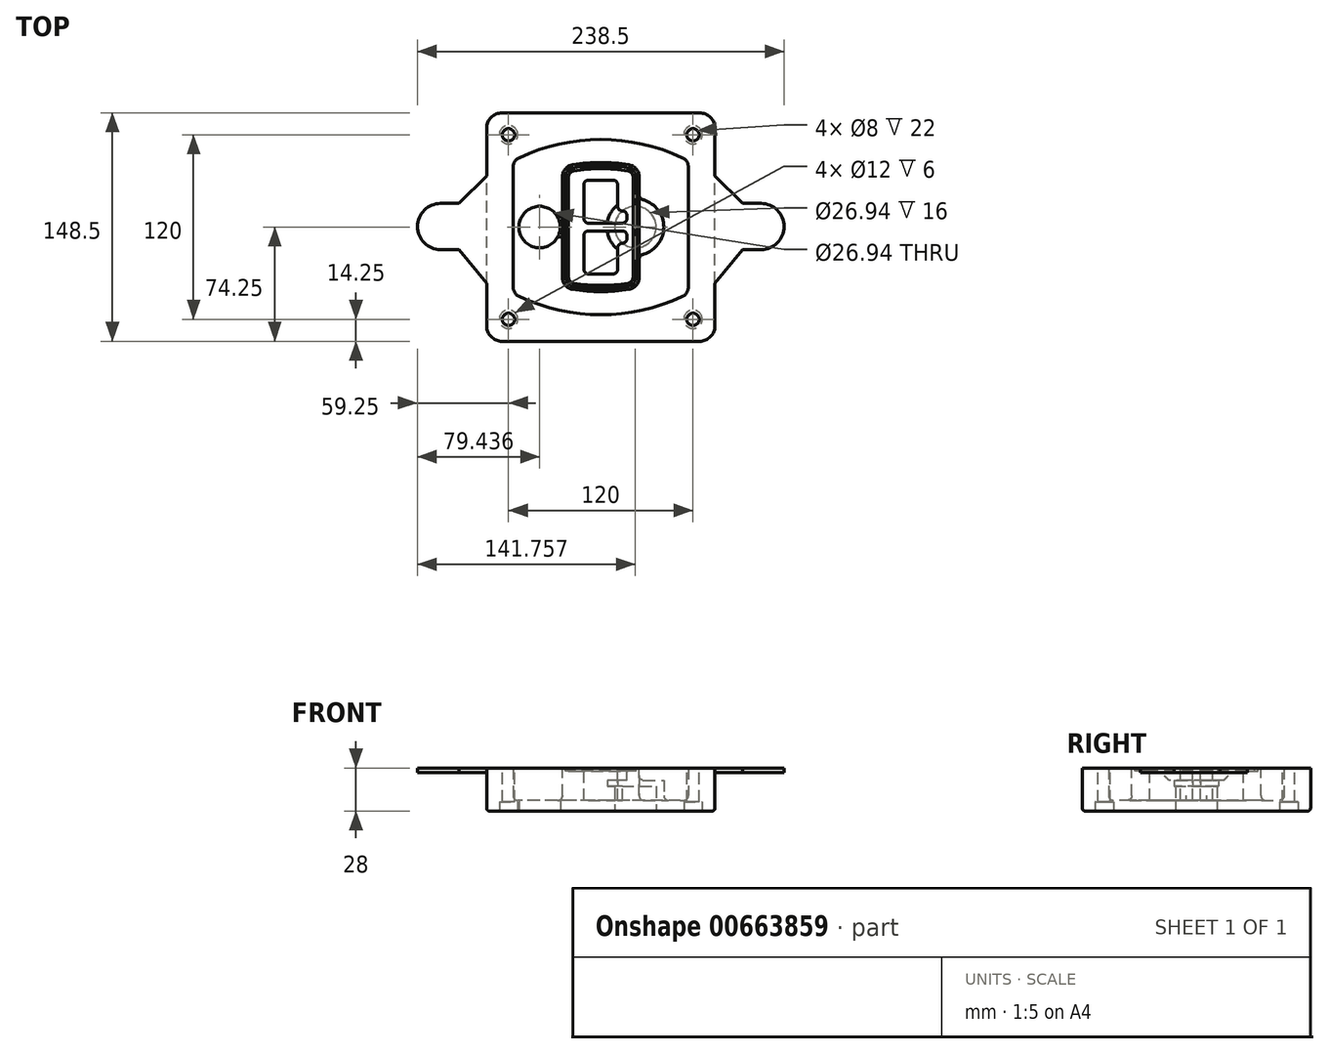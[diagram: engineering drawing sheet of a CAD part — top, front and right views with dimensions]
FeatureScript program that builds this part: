
annotation { "Feature Type Name" : "Feature", "Feature Type Description" : "" }
export const myFeature = defineFeature(function(context is Context, id is Id, definition is map)
    precondition{}
    {
        {
            var Q0;
            Q0=qCreatedBy(makeId("Top.planeOp"),FACE);
            var sketch = newSketch(context, id + "F0", { "sketchPlane" : qUnion([Q0])});
            skPoint(sketch, "E0.rect.middle", {"position": v(0, 0) * mm});
            skLineSegment(sketch, "E1.bottom", {"start": v(-64.25, -74.25) * mm, "end": v(64.25, -74.25) * mm});
            skLineSegment(sketch, "E1.top", {"start": v(-64.25, 74.25) * mm, "end": v(64.25, 74.25) * mm});
            skLineSegment(sketch, "E1.left", {"start": v(-74.25, -64.25) * mm, "end": v(-74.25, 64.25) * mm});
            skLineSegment(sketch, "E1.right", {"start": v(74.25, -64.25) * mm, "end": v(74.25, 64.25) * mm});
            skLineSegment(sketch, "E2", {"start": v(-74.25, 74.25) * mm, "end": v(74.25, -74.25) * mm, "construction": true});
            skLineSegment(sketch, "E3", {"start": v(74.25, 74.25) * mm, "end": v(-74.25, -74.25) * mm, "construction": true});
            skCircle(sketch, "E4", {"center": v(-60, 60) * mm, "radius": 4 * mm});
            skCircle(sketch, "E5", {"center": v(60, 60) * mm, "radius": 4 * mm});
            skCircle(sketch, "E6", {"center": v(60, -60) * mm, "radius": 4 * mm});
            skCircle(sketch, "E7", {"center": v(-60, -60) * mm, "radius": 4 * mm});
            skLineSegment(sketch, "E8", {"start": v(-60, 60) * mm, "end": v(60, 60) * mm, "construction": true});
            skLineSegment(sketch, "E9", {"start": v(60, 60) * mm, "end": v(60, -60) * mm, "construction": true});
            skLineSegment(sketch, "E10", {"start": v(60, -60) * mm, "end": v(-60, -60) * mm, "construction": true});
            skLineSegment(sketch, "E11", {"start": v(-60, -60) * mm, "end": v(-60, 60) * mm, "construction": true});
            skLineSegment(sketch, "E12", {"start": v(-60, 38.83) * mm, "end": v(-60, -38.83) * mm});
            skLineSegment(sketch, "E13", {"start": v(60, 38.83) * mm, "end": v(60, -38.83) * mm});
            skArc(sketch, "E14", {"start": v(54.26, 47.88) * mm, "mid": v(0, 60) * mm, "end": v(-54.26, 47.88) * mm});
            skArc(sketch, "E15", {"start": v(-54.26, -47.88) * mm, "mid": v(0, -60) * mm, "end": v(54.26, -47.88) * mm});
            skLineSegment(sketch, "E16", {"start": v(-60, 0) * mm, "end": v(60, 0) * mm, "construction": true});
            skPoint(sketch, "E17.visualSharp", {"position": v(-60, -45) * mm});
            skArc(sketch, "E17.filletArc", {"start": v(-60, -38.83) * mm, "mid": v(-58.44, -44.2) * mm, "end": v(-54.26, -47.88) * mm});
            skPoint(sketch, "E18.visualSharp", {"position": v(-60, 45) * mm});
            skArc(sketch, "E18.filletArc", {"start": v(-54.26, 47.88) * mm, "mid": v(-58.44, 44.2) * mm, "end": v(-60, 38.83) * mm});
            skPoint(sketch, "E19.visualSharp", {"position": v(60, 45) * mm});
            skArc(sketch, "E19.filletArc", {"start": v(60, 38.83) * mm, "mid": v(58.44, 44.2) * mm, "end": v(54.26, 47.88) * mm});
            skPoint(sketch, "E20.visualSharp", {"position": v(60, -45) * mm});
            skArc(sketch, "E20.filletArc", {"start": v(54.26, -47.88) * mm, "mid": v(58.44, -44.2) * mm, "end": v(60, -38.83) * mm});
            skPoint(sketch, "E21.visualSharp", {"position": v(-74.25, 74.25) * mm});
            skArc(sketch, "E21.filletArc", {"start": v(-64.25, 74.25) * mm, "mid": v(-71.32, 71.32) * mm, "end": v(-74.25, 64.25) * mm});
            skPoint(sketch, "E22.visualSharp", {"position": v(74.25, 74.25) * mm});
            skArc(sketch, "E22.filletArc", {"start": v(74.25, 64.25) * mm, "mid": v(71.32, 71.32) * mm, "end": v(64.25, 74.25) * mm});
            skPoint(sketch, "E23.visualSharp", {"position": v(74.25, -74.25) * mm});
            skArc(sketch, "E23.filletArc", {"start": v(64.25, -74.25) * mm, "mid": v(71.32, -71.32) * mm, "end": v(74.25, -64.25) * mm});
            skPoint(sketch, "E24.visualSharp", {"position": v(-74.25, -74.25) * mm});
            skArc(sketch, "E24.filletArc", {"start": v(-74.25, -64.25) * mm, "mid": v(-71.32, -71.32) * mm, "end": v(-64.25, -74.25) * mm});
            skArc(sketch, "E25.0", {"start": v(57, 38.83) * mm, "mid": v(55.9, 42.58) * mm, "end": v(52.98, 45.17) * mm});
            skLineSegment(sketch, "E25.1", {"start": v(57, 38.83) * mm, "end": v(57, -38.83) * mm});
            skArc(sketch, "E25.2", {"start": v(52.98, -45.17) * mm, "mid": v(55.9, -42.58) * mm, "end": v(57, -38.83) * mm});
            skArc(sketch, "E25.3", {"start": v(-52.98, -45.17) * mm, "mid": v(0, -57) * mm, "end": v(52.98, -45.17) * mm});
            skArc(sketch, "E25.4", {"start": v(-57, -38.83) * mm, "mid": v(-55.9, -42.58) * mm, "end": v(-52.98, -45.17) * mm});
            skArc(sketch, "E25.5", {"start": v(52.98, 45.17) * mm, "mid": v(0, 57) * mm, "end": v(-52.98, 45.17) * mm});
            skLineSegment(sketch, "E25.6", {"start": v(-57, 38.83) * mm, "end": v(-57, -38.83) * mm});
            skArc(sketch, "E25.7", {"start": v(-52.98, 45.17) * mm, "mid": v(-55.9, 42.58) * mm, "end": v(-57, 38.83) * mm});
            skArc(sketch, "E26.0", {"start": v(-55.96, 51.5) * mm, "mid": v(-61.82, 46.33) * mm, "end": v(-64, 38.83) * mm});
            skArc(sketch, "E26.1", {"start": v(55.96, 51.5) * mm, "mid": v(0, 64) * mm, "end": v(-55.96, 51.5) * mm});
            skArc(sketch, "E26.2", {"start": v(64, 38.83) * mm, "mid": v(61.82, 46.33) * mm, "end": v(55.96, 51.5) * mm});
            skLineSegment(sketch, "E26.3", {"start": v(64, 38.83) * mm, "end": v(64, -38.83) * mm});
            skArc(sketch, "E26.4", {"start": v(55.96, -51.5) * mm, "mid": v(61.82, -46.33) * mm, "end": v(64, -38.83) * mm});
            skLineSegment(sketch, "E26.5", {"start": v(-64, 38.83) * mm, "end": v(-64, -38.83) * mm});
            skArc(sketch, "E26.6", {"start": v(-55.96, -51.5) * mm, "mid": v(0, -64) * mm, "end": v(55.96, -51.5) * mm});
            skArc(sketch, "E26.7", {"start": v(-64, -38.83) * mm, "mid": v(-61.82, -46.33) * mm, "end": v(-55.96, -51.5) * mm});
            skSolve(sketch);
        }
        {
            var Q0;
            Q0=makeQuery(id+"F0.imprint","IMPRINT",FACE,{"disambiguationData":[TD([[makeQuery(id+"F0.imprint","IMPRINT",EDGE,{"derivedFrom":sQuery(id+"F0.wireOp",EDGE,"E1.bottom")}),1.0]])]});
            var Q1;
            Q1=makeQuery(id+"F0.imprint","IMPRINT",FACE,{"disambiguationData":[TD([[makeQuery(id+"F0.imprint","IMPRINT",EDGE,{"derivedFrom":sQuery(id+"F0.wireOp",EDGE,"E12")}),1.0]])]});
            var Q2;
            Q2=makeQuery(id+"F0.imprint","IMPRINT",FACE,{"disambiguationData":[TD([[makeQuery(id+"F0.imprint","IMPRINT",EDGE,{"derivedFrom":sQuery(id+"F0.wireOp",EDGE,"E25.0")}),1.0]])]});
            var Q3;
            Q3=makeQuery(id+"F0.imprint","IMPRINT",FACE,{"disambiguationData":[TD([[makeQuery(id+"F0.imprint","IMPRINT",EDGE,{"derivedFrom":sQuery(id+"F0.wireOp",EDGE,"E12")}),-1.0]])]});
            extrude(context, id + "F1", {"entities" : qUnion([Q0, Q1, Q2, Q3]), "oppositeDirection" : true, "depth" : 25 * mm});
        }
        {
            var Q0;
            Q0=makeQuery(id+"F0.imprint","IMPRINT",FACE,{"disambiguationData":[TD([[makeQuery(id+"F0.imprint","IMPRINT",EDGE,{"derivedFrom":sQuery(id+"F0.wireOp",EDGE,"E12")}),1.0]])]});
            extrude(context, id + "F2", {"entities" : qUnion([Q0]), "operationType" : NewBodyOperationType.ADD, "depth" : 3 * mm, "offsetDistance" : 25 * mm});
        }
        {
            var Q0;
            Q0=makeQuery(id+"F0.imprint","IMPRINT",FACE,{"disambiguationData":[TD([[makeQuery(id+"F0.imprint","IMPRINT",EDGE,{"derivedFrom":sQuery(id+"F0.wireOp",EDGE,"E25.0")}),1.0]])]});
            extrude(context, id + "F3", {"entities" : qUnion([Q0]), "operationType" : NewBodyOperationType.REMOVE, "oppositeDirection" : true, "depth" : 18 * mm});
        }
        {
            var Q0;
            Q0=makeQuery(id+"F2.opExtrude","CAP_FACE",FACE,{"disambiguationData":[OSD([sQuery(id+"F0.wireOp",EDGE,"E12"),sQuery(id+"F0.wireOp",EDGE,"E13"),sQuery(id+"F0.wireOp",EDGE,"E14"),sQuery(id+"F0.wireOp",EDGE,"E15"),sQuery(id+"F0.wireOp",EDGE,"E17.filletArc"),sQuery(id+"F0.wireOp",EDGE,"E18.filletArc"),sQuery(id+"F0.wireOp",EDGE,"E19.filletArc"),sQuery(id+"F0.wireOp",EDGE,"E20.filletArc"),sQuery(id+"F0.wireOp",EDGE,"E25.0"),sQuery(id+"F0.wireOp",EDGE,"E25.1"),sQuery(id+"F0.wireOp",EDGE,"E25.2"),sQuery(id+"F0.wireOp",EDGE,"E25.3"),sQuery(id+"F0.wireOp",EDGE,"E25.4"),sQuery(id+"F0.wireOp",EDGE,"E25.5"),sQuery(id+"F0.wireOp",EDGE,"E25.6"),sQuery(id+"F0.wireOp",EDGE,"E25.7")])],"isStart":false});
            var sketch = newSketch(context, id + "F4", { "sketchPlane" : qUnion([Q0])});
            skArc(sketch, "E27.0", {"start": v(-18.34, -40.45) * mm, "mid": v(0, -42) * mm, "end": v(18.34, -40.45) * mm});
            skArc(sketch, "E28.0", {"start": v(18.34, 40.45) * mm, "mid": v(0, 42) * mm, "end": v(-18.34, 40.45) * mm});
            skLineSegment(sketch, "E29", {"start": v(-25, 32.57) * mm, "end": v(-25, -32.57) * mm});
            skLineSegment(sketch, "E30", {"start": v(25, 32.57) * mm, "end": v(25, -32.57) * mm});
            skLineSegment(sketch, "E31", {"start": v(-25, 39.1) * mm, "end": v(25, 39.1) * mm, "construction": true});
            skLineSegment(sketch, "E32", {"start": v(-25, -39.1) * mm, "end": v(25, -39.1) * mm, "construction": true});
            skPoint(sketch, "E33.visualSharp", {"position": v(-25, 39.1) * mm});
            skArc(sketch, "E33.filletArc", {"start": v(-18.34, 40.45) * mm, "mid": v(-23.11, 37.73) * mm, "end": v(-25, 32.57) * mm});
            skPoint(sketch, "E34.visualSharp", {"position": v(25, 39.1) * mm});
            skArc(sketch, "E34.filletArc", {"start": v(25, 32.57) * mm, "mid": v(23.11, 37.73) * mm, "end": v(18.34, 40.45) * mm});
            skPoint(sketch, "E35.visualSharp", {"position": v(25, -39.1) * mm});
            skArc(sketch, "E35.filletArc", {"start": v(18.34, -40.45) * mm, "mid": v(23.11, -37.73) * mm, "end": v(25, -32.57) * mm});
            skPoint(sketch, "E36.visualSharp", {"position": v(-25, -39.1) * mm});
            skArc(sketch, "E36.filletArc", {"start": v(-25, -32.57) * mm, "mid": v(-23.11, -37.73) * mm, "end": v(-18.34, -40.45) * mm});
            skArc(sketch, "E37.0", {"start": v(52.98, 45.17) * mm, "mid": v(0, 57) * mm, "end": v(-52.98, 45.17) * mm});
            skArc(sketch, "E37.1", {"start": v(-52.98, 45.17) * mm, "mid": v(-55.9, 42.58) * mm, "end": v(-57, 38.83) * mm});
            skLineSegment(sketch, "E37.2", {"start": v(-57, 38.83) * mm, "end": v(-57, -38.83) * mm});
            skArc(sketch, "E37.3", {"start": v(-57, -38.83) * mm, "mid": v(-55.9, -42.58) * mm, "end": v(-52.98, -45.17) * mm});
            skArc(sketch, "E37.4", {"start": v(-52.98, -45.17) * mm, "mid": v(0, -57) * mm, "end": v(52.98, -45.17) * mm});
            skArc(sketch, "E37.5", {"start": v(52.98, -45.17) * mm, "mid": v(55.9, -42.58) * mm, "end": v(57, -38.83) * mm});
            skLineSegment(sketch, "E37.6", {"start": v(57, 38.83) * mm, "end": v(57, -38.83) * mm});
            skArc(sketch, "E37.7", {"start": v(57, 38.83) * mm, "mid": v(55.9, 42.58) * mm, "end": v(52.98, 45.17) * mm});
            skLineSegment(sketch, "E38.0", {"start": v(23, 32.57) * mm, "end": v(23, -32.57) * mm});
            skArc(sketch, "E38.1", {"start": v(18, -38.48) * mm, "mid": v(21.58, -36.44) * mm, "end": v(23, -32.57) * mm});
            skArc(sketch, "E38.2", {"start": v(-18, -38.48) * mm, "mid": v(0, -40) * mm, "end": v(18, -38.48) * mm});
            skArc(sketch, "E38.3", {"start": v(-23, -32.57) * mm, "mid": v(-21.58, -36.44) * mm, "end": v(-18, -38.48) * mm});
            skLineSegment(sketch, "E38.4", {"start": v(-23, 32.57) * mm, "end": v(-23, -32.57) * mm});
            skArc(sketch, "E38.5", {"start": v(23, 32.57) * mm, "mid": v(21.58, 36.44) * mm, "end": v(18, 38.48) * mm});
            skArc(sketch, "E38.6", {"start": v(-18, 38.48) * mm, "mid": v(-21.58, 36.44) * mm, "end": v(-23, 32.57) * mm});
            skArc(sketch, "E38.7", {"start": v(18, 38.48) * mm, "mid": v(0, 40) * mm, "end": v(-18, 38.48) * mm});
            skArc(sketch, "E39.0", {"start": v(21, 32.57) * mm, "mid": v(20.06, 35.15) * mm, "end": v(17.67, 36.5) * mm});
            skLineSegment(sketch, "E39.1", {"start": v(21, 32.57) * mm, "end": v(21, -32.57) * mm});
            skArc(sketch, "E39.2", {"start": v(17.67, -36.5) * mm, "mid": v(20.06, -35.15) * mm, "end": v(21, -32.57) * mm});
            skArc(sketch, "E39.3", {"start": v(-17.67, -36.5) * mm, "mid": v(0, -38) * mm, "end": v(17.67, -36.5) * mm});
            skArc(sketch, "E39.4", {"start": v(-21, -32.57) * mm, "mid": v(-20.06, -35.15) * mm, "end": v(-17.67, -36.5) * mm});
            skArc(sketch, "E39.5", {"start": v(17.67, 36.5) * mm, "mid": v(0, 38) * mm, "end": v(-17.67, 36.5) * mm});
            skLineSegment(sketch, "E39.6", {"start": v(-21, 32.57) * mm, "end": v(-21, -32.57) * mm});
            skArc(sketch, "E39.7", {"start": v(-17.67, 36.5) * mm, "mid": v(-20.06, 35.15) * mm, "end": v(-21, 32.57) * mm});
            skLineSegment(sketch, "E40", {"start": v(-25, 0) * mm, "end": v(25, 0) * mm, "construction": true});
            skLineSegment(sketch, "E41", {"start": v(-11, 5.5) * mm, "end": v(-11, 27.5) * mm});
            skLineSegment(sketch, "E42", {"start": v(-8, 30.5) * mm, "end": v(8, 30.5) * mm});
            skLineSegment(sketch, "E43", {"start": v(11, 27.5) * mm, "end": v(11, 13.5) * mm});
            skLineSegment(sketch, "E44", {"start": v(14, 10.5) * mm, "end": v(14, 10.5) * mm});
            skLineSegment(sketch, "E45", {"start": v(17, 7.5) * mm, "end": v(17, 5.5) * mm});
            skLineSegment(sketch, "E46", {"start": v(14, 2.5) * mm, "end": v(-8, 2.5) * mm});
            skPoint(sketch, "E47.visualSharp", {"position": v(-11, 30.5) * mm});
            skArc(sketch, "E47.filletArc", {"start": v(-8, 30.5) * mm, "mid": v(-10.12, 29.62) * mm, "end": v(-11, 27.5) * mm});
            skPoint(sketch, "E48.visualSharp", {"position": v(11, 30.5) * mm});
            skArc(sketch, "E48.filletArc", {"start": v(11, 27.5) * mm, "mid": v(10.12, 29.62) * mm, "end": v(8, 30.5) * mm});
            skPoint(sketch, "E49.visualSharp", {"position": v(11, 10.5) * mm});
            skArc(sketch, "E49.filletArc", {"start": v(11, 13.5) * mm, "mid": v(11.88, 11.38) * mm, "end": v(14, 10.5) * mm});
            skPoint(sketch, "E50.visualSharp", {"position": v(17, 10.5) * mm});
            skArc(sketch, "E50.filletArc", {"start": v(17, 7.5) * mm, "mid": v(16.12, 9.62) * mm, "end": v(14, 10.5) * mm});
            skPoint(sketch, "E51.visualSharp", {"position": v(17, 2.5) * mm});
            skArc(sketch, "E51.filletArc", {"start": v(14, 2.5) * mm, "mid": v(16.12, 3.38) * mm, "end": v(17, 5.5) * mm});
            skPoint(sketch, "E52.visualSharp", {"position": v(-11, 2.5) * mm});
            skArc(sketch, "E52.filletArc", {"start": v(-11, 5.5) * mm, "mid": v(-10.12, 3.38) * mm, "end": v(-8, 2.5) * mm});
            skLineSegment(sketch, "E53.0.MirrorCS", {"start": v(14, -2.5) * mm, "end": v(-8, -2.5) * mm});
            skArc(sketch, "E54.0.MirrorCS", {"start": v(-11, -5.5) * mm, "mid": v(-10.12, -3.38) * mm, "end": v(-8, -2.5) * mm});
            skLineSegment(sketch, "E55.0.MirrorCS", {"start": v(-11, -5.5) * mm, "end": v(-11, -27.5) * mm});
            skArc(sketch, "E56.0.MirrorCS", {"start": v(-8, -30.5) * mm, "mid": v(-10.12, -29.62) * mm, "end": v(-11, -27.5) * mm});
            skLineSegment(sketch, "E57.0.MirrorCS", {"start": v(-8, -30.5) * mm, "end": v(8, -30.5) * mm});
            skArc(sketch, "E58.0.MirrorCS", {"start": v(11, -27.5) * mm, "mid": v(10.12, -29.62) * mm, "end": v(8, -30.5) * mm});
            skLineSegment(sketch, "E59.0.MirrorCS", {"start": v(11, -27.5) * mm, "end": v(11, -13.5) * mm});
            skArc(sketch, "E60.0.MirrorCS", {"start": v(11, -13.5) * mm, "mid": v(11.88, -11.38) * mm, "end": v(14, -10.5) * mm});
            skArc(sketch, "E61.0.MirrorCS", {"start": v(17, -7.5) * mm, "mid": v(16.12, -9.62) * mm, "end": v(14, -10.5) * mm});
            skLineSegment(sketch, "E62.0.MirrorCS", {"start": v(17, -7.5) * mm, "end": v(17, -5.5) * mm});
            skArc(sketch, "E63.0.MirrorCS", {"start": v(14, -2.5) * mm, "mid": v(16.12, -3.38) * mm, "end": v(17, -5.5) * mm});
            skSolve(sketch);
        }
        {
            var Q0;
            Q0=makeQuery(id+"F4.imprint","IMPRINT",FACE,{"disambiguationData":[TD([[makeQuery(id+"F4.imprint","IMPRINT",EDGE,{"derivedFrom":sQuery(id+"F4.wireOp",EDGE,"E27.0")}),1.0]])]});
            var Q1;
            Q1=makeQuery(id+"F4.imprint","IMPRINT",FACE,{"disambiguationData":[TD([[makeQuery(id+"F4.imprint","IMPRINT",EDGE,{"derivedFrom":sQuery(id+"F4.wireOp",EDGE,"E38.0")}),-1.0]])]});
            var Q2;
            Q2=makeQuery(id+"F4.imprint","IMPRINT",FACE,{"disambiguationData":[TD([[makeQuery(id+"F4.imprint","IMPRINT",EDGE,{"derivedFrom":sQuery(id+"F4.wireOp",EDGE,"E39.0")}),1.0]])]});
            extrude(context, id + "F5", {"entities" : qUnion([Q0, Q1, Q2]), "operationType" : NewBodyOperationType.ADD, "endBound" : BoundingType.UP_TO_NEXT, "oppositeDirection" : true, "depth" : 25 * mm});
        }
        {
            var Q0;
            Q0=makeQuery(id+"F4.imprint","IMPRINT",FACE,{"disambiguationData":[TD([[makeQuery(id+"F4.imprint","IMPRINT",EDGE,{"derivedFrom":sQuery(id+"F4.wireOp",EDGE,"E38.0")}),-1.0]])]});
            extrude(context, id + "F6", {"entities" : qUnion([Q0]), "operationType" : NewBodyOperationType.REMOVE, "oppositeDirection" : true, "depth" : 2 * mm});
        }
        {
            var Q0;
            Q0=makeQuery(id+"F1.opExtrude","CAP_FACE",FACE,{"disambiguationData":[OSD([sQuery(id+"F0.wireOp",EDGE,"E1.bottom"),sQuery(id+"F0.wireOp",EDGE,"E1.top"),sQuery(id+"F0.wireOp",EDGE,"E1.left"),sQuery(id+"F0.wireOp",EDGE,"E1.right"),sQuery(id+"F0.wireOp",EDGE,"E4"),sQuery(id+"F0.wireOp",EDGE,"E5"),sQuery(id+"F0.wireOp",EDGE,"E6"),sQuery(id+"F0.wireOp",EDGE,"E7"),sQuery(id+"F0.wireOp",EDGE,"E21.filletArc"),sQuery(id+"F0.wireOp",EDGE,"E22.filletArc"),sQuery(id+"F0.wireOp",EDGE,"E23.filletArc"),sQuery(id+"F0.wireOp",EDGE,"E24.filletArc")])],"isStart":false});
            var sketch = newSketch(context, id + "F7", { "sketchPlane" : qUnion([Q0])});
            skCircle(sketch, "E64", {"center": v(22.5, 0) * mm, "radius": 13.47 * mm});
            skCircle(sketch, "E65", {"center": v(-39.81, 0) * mm, "radius": 13.47 * mm});
            skLineSegment(sketch, "E66", {"start": v(74.25, 0) * mm, "end": v(-74.25, 0) * mm});
            skCircle(sketch, "E67", {"center": v(22.5, 0) * mm, "radius": 18.47 * mm});
            skCircle(sketch, "E68", {"center": v(60, -60) * mm, "radius": 6 * mm});
            skCircle(sketch, "E69", {"center": v(-60, -60) * mm, "radius": 6 * mm});
            skCircle(sketch, "E70", {"center": v(-60, 60) * mm, "radius": 6 * mm});
            skCircle(sketch, "E71", {"center": v(60, 60) * mm, "radius": 6 * mm});
            skSolve(sketch);
        }
        {
            var Q0;
            {var subQ1=sQuery(id+"F7.wireOp",EDGE,"E66");var subQ4=sQuery(id+"F7.wireOp",EDGE,"E64");var subQ6=makeQuery(id+"F7.imprint","INTERSECT",VERTEX,{"disambiguationData":[OD(0.0)],"derivedFrom":[subQ4,subQ1]});Q0=makeQuery(id+"F7.imprint","IMPRINT",FACE,{"disambiguationData":[TD([[makeQuery(id+"F7.imprint","IMPRINT",EDGE,{"disambiguationData":[TD([[subQ6,-1.0]])],"derivedFrom":subQ4}),-1.0]])]});}
            var Q1;
            {var subQ0=sQuery(id+"F7.wireOp",EDGE,"E66");var subQ1=sQuery(id+"F7.wireOp",EDGE,"E64");var subQ3=makeQuery(id+"F7.imprint","INTERSECT",VERTEX,{"disambiguationData":[OD(0.0)],"derivedFrom":[subQ1,subQ0]});Q1=makeQuery(id+"F7.imprint","IMPRINT",FACE,{"disambiguationData":[TD([[makeQuery(id+"F7.imprint","IMPRINT",EDGE,{"disambiguationData":[TD([[subQ3,-1.0]])],"derivedFrom":subQ1}),1.0]])]});}
            var Q2;
            {var subQ0=sQuery(id+"F7.wireOp",EDGE,"E66");var subQ1=sQuery(id+"F7.wireOp",EDGE,"E64");var subQ3=makeQuery(id+"F7.imprint","INTERSECT",VERTEX,{"disambiguationData":[OD(0.0)],"derivedFrom":[subQ1,subQ0]});Q2=makeQuery(id+"F7.imprint","IMPRINT",FACE,{"disambiguationData":[TD([[makeQuery(id+"F7.imprint","IMPRINT",EDGE,{"disambiguationData":[TD([[subQ3,1.0]])],"derivedFrom":subQ1}),1.0]])]});}
            var Q3;
            {var subQ1=sQuery(id+"F7.wireOp",EDGE,"E66");var subQ4=sQuery(id+"F7.wireOp",EDGE,"E64");var subQ6=makeQuery(id+"F7.imprint","INTERSECT",VERTEX,{"disambiguationData":[OD(0.0)],"derivedFrom":[subQ4,subQ1]});Q3=makeQuery(id+"F7.imprint","IMPRINT",FACE,{"disambiguationData":[TD([[makeQuery(id+"F7.imprint","IMPRINT",EDGE,{"disambiguationData":[TD([[subQ6,1.0]])],"derivedFrom":subQ4}),-1.0]])]});}
            extrude(context, id + "F8", {"entities" : qUnion([Q0, Q1, Q2, Q3]), "operationType" : NewBodyOperationType.ADD, "oppositeDirection" : true, "depth" : 20 * mm});
        }
        {
            var Q0;
            {var subQ0=sQuery(id+"F7.wireOp",EDGE,"E66");var subQ1=sQuery(id+"F7.wireOp",EDGE,"E64");var subQ3=makeQuery(id+"F7.imprint","INTERSECT",VERTEX,{"disambiguationData":[OD(0.0)],"derivedFrom":[subQ1,subQ0]});Q0=makeQuery(id+"F7.imprint","IMPRINT",FACE,{"disambiguationData":[TD([[makeQuery(id+"F7.imprint","IMPRINT",EDGE,{"disambiguationData":[TD([[subQ3,-1.0]])],"derivedFrom":subQ1}),1.0]])]});}
            var Q1;
            {var subQ0=sQuery(id+"F7.wireOp",EDGE,"E66");var subQ1=sQuery(id+"F7.wireOp",EDGE,"E64");var subQ3=makeQuery(id+"F7.imprint","INTERSECT",VERTEX,{"disambiguationData":[OD(0.0)],"derivedFrom":[subQ1,subQ0]});Q1=makeQuery(id+"F7.imprint","IMPRINT",FACE,{"disambiguationData":[TD([[makeQuery(id+"F7.imprint","IMPRINT",EDGE,{"disambiguationData":[TD([[subQ3,1.0]])],"derivedFrom":subQ1}),1.0]])]});}
            extrude(context, id + "F9", {"entities" : qUnion([Q0, Q1]), "operationType" : NewBodyOperationType.REMOVE, "oppositeDirection" : true, "depth" : 16 * mm});
        }
        {
            var Q0;
            {var subQ0=sQuery(id+"F7.wireOp",EDGE,"E66");var subQ1=sQuery(id+"F7.wireOp",EDGE,"E65");var subQ3=makeQuery(id+"F7.imprint","INTERSECT",VERTEX,{"disambiguationData":[OD(0.0)],"derivedFrom":[subQ1,subQ0]});Q0=makeQuery(id+"F7.imprint","IMPRINT",FACE,{"disambiguationData":[TD([[makeQuery(id+"F7.imprint","IMPRINT",EDGE,{"disambiguationData":[TD([[subQ3,-1.0]])],"derivedFrom":subQ1}),1.0]])]});}
            var Q1;
            {var subQ0=sQuery(id+"F7.wireOp",EDGE,"E66");var subQ1=sQuery(id+"F7.wireOp",EDGE,"E65");var subQ3=makeQuery(id+"F7.imprint","INTERSECT",VERTEX,{"disambiguationData":[OD(0.0)],"derivedFrom":[subQ1,subQ0]});Q1=makeQuery(id+"F7.imprint","IMPRINT",FACE,{"disambiguationData":[TD([[makeQuery(id+"F7.imprint","IMPRINT",EDGE,{"disambiguationData":[TD([[subQ3,1.0]])],"derivedFrom":subQ1}),1.0]])]});}
            extrude(context, id + "F10", {"entities" : qUnion([Q0, Q1]), "operationType" : NewBodyOperationType.REMOVE, "oppositeDirection" : true, "depth" : 25 * mm});
        }
        {
            var Q0;
            Q0=makeQuery(id+"F7.imprint","IMPRINT",FACE,{"disambiguationData":[TD([[makeQuery(id+"F7.imprint","IMPRINT",EDGE,{"derivedFrom":sQuery(id+"F7.wireOp",EDGE,"E68")}),1.0]])]});
            var Q1;
            Q1=makeQuery(id+"F7.imprint","IMPRINT",FACE,{"disambiguationData":[TD([[makeQuery(id+"F7.imprint","IMPRINT",EDGE,{"derivedFrom":makeQuery(id+"F1.opExtrude","CAP_EDGE",EDGE,{"disambiguationData":[OSD([sQuery(id+"F0.wireOp",EDGE,"E5")])],"isStart":false})}),-1.0]])]});
            var Q2;
            Q2=makeQuery(id+"F7.imprint","IMPRINT",FACE,{"disambiguationData":[TD([[makeQuery(id+"F7.imprint","IMPRINT",EDGE,{"derivedFrom":sQuery(id+"F7.wireOp",EDGE,"E69")}),1.0]])]});
            var Q3;
            Q3=makeQuery(id+"F7.imprint","IMPRINT",FACE,{"disambiguationData":[TD([[makeQuery(id+"F7.imprint","IMPRINT",EDGE,{"derivedFrom":makeQuery(id+"F1.opExtrude","CAP_EDGE",EDGE,{"disambiguationData":[OSD([sQuery(id+"F0.wireOp",EDGE,"E4")])],"isStart":false})}),-1.0]])]});
            var Q4;
            Q4=makeQuery(id+"F7.imprint","IMPRINT",FACE,{"disambiguationData":[TD([[makeQuery(id+"F7.imprint","IMPRINT",EDGE,{"derivedFrom":sQuery(id+"F7.wireOp",EDGE,"E70")}),1.0]])]});
            var Q5;
            Q5=makeQuery(id+"F7.imprint","IMPRINT",FACE,{"disambiguationData":[TD([[makeQuery(id+"F7.imprint","IMPRINT",EDGE,{"derivedFrom":makeQuery(id+"F1.opExtrude","CAP_EDGE",EDGE,{"disambiguationData":[OSD([sQuery(id+"F0.wireOp",EDGE,"E7")])],"isStart":false})}),-1.0]])]});
            var Q6;
            Q6=makeQuery(id+"F7.imprint","IMPRINT",FACE,{"disambiguationData":[TD([[makeQuery(id+"F7.imprint","IMPRINT",EDGE,{"derivedFrom":sQuery(id+"F7.wireOp",EDGE,"E71")}),1.0]])]});
            var Q7;
            Q7=makeQuery(id+"F7.imprint","IMPRINT",FACE,{"disambiguationData":[TD([[makeQuery(id+"F7.imprint","IMPRINT",EDGE,{"derivedFrom":makeQuery(id+"F1.opExtrude","CAP_EDGE",EDGE,{"disambiguationData":[OSD([sQuery(id+"F0.wireOp",EDGE,"E6")])],"isStart":false})}),-1.0]])]});
            extrude(context, id + "F11", {"entities" : qUnion([Q0, Q1, Q2, Q3, Q4, Q5, Q6, Q7]), "operationType" : NewBodyOperationType.REMOVE, "oppositeDirection" : true, "depth" : 6 * mm});
        }
        {
            var Q0;
            Q0=makeQuery(id+"F9.boolean.opBoolean","COPY",FACE,{"derivedFrom":makeQuery(id+"F9.opExtrude","CAP_FACE",FACE,{"disambiguationData":[OSD([sQuery(id+"F7.wireOp",EDGE,"E64")])],"isStart":false})});
            var sketch = newSketch(context, id + "F12", { "sketchPlane" : qUnion([Q0])});
            skArc(sketch, "E72.0", {"start": v(11, 14.45) * mm, "mid": v(6.45, 9.13) * mm, "end": v(4.2, 2.5) * mm});
            skArc(sketch, "E72.1", {"start": v(4.2, -2.5) * mm, "mid": v(6.45, -9.13) * mm, "end": v(11, -14.45) * mm});
            skLineSegment(sketch, "E73", {"start": v(4.2, -2.5) * mm, "end": v(14, -2.5) * mm});
            skLineSegment(sketch, "E74.0", {"start": v(14, 2.5) * mm, "end": v(4.2, 2.5) * mm});
            skArc(sketch, "E74.1", {"start": v(14, 2.5) * mm, "mid": v(16.12, 3.38) * mm, "end": v(17, 5.5) * mm});
            skLineSegment(sketch, "E74.2", {"start": v(17, 7.5) * mm, "end": v(17, 5.5) * mm});
            skArc(sketch, "E74.3", {"start": v(17, 7.5) * mm, "mid": v(16.12, 9.62) * mm, "end": v(14, 10.5) * mm});
            skArc(sketch, "E74.4", {"start": v(11, 13.5) * mm, "mid": v(11.88, 11.38) * mm, "end": v(14, 10.5) * mm});
            skLineSegment(sketch, "E74.5", {"start": v(11, 14.45) * mm, "end": v(11, 13.5) * mm});
            skLineSegment(sketch, "E74.7", {"start": v(14, -2.5) * mm, "end": v(4.2, -2.5) * mm});
            skArc(sketch, "E74.8", {"start": v(14, -2.5) * mm, "mid": v(16.12, -3.38) * mm, "end": v(17, -5.5) * mm});
            skLineSegment(sketch, "E74.9", {"start": v(17, -7.5) * mm, "end": v(17, -5.5) * mm});
            skArc(sketch, "E74.10", {"start": v(17, -7.5) * mm, "mid": v(16.12, -9.62) * mm, "end": v(14, -10.5) * mm});
            skArc(sketch, "E74.11", {"start": v(11, -13.5) * mm, "mid": v(11.88, -11.38) * mm, "end": v(14, -10.5) * mm});
            skLineSegment(sketch, "E74.12", {"start": v(11, -14.45) * mm, "end": v(11, -13.5) * mm});
            skPoint(sketch, "E75.orphan", {"position": v(11, -27.5) * mm});
            skPoint(sketch, "E76.orphan", {"position": v(-8, -2.5) * mm});
            skPoint(sketch, "E77.orphan", {"position": v(-8, 2.5) * mm});
            skPoint(sketch, "E78.orphan", {"position": v(11, 27.5) * mm});
            skSolve(sketch);
        }
        {
            var Q0;
            {var subQ7=sQuery(id+"F12.wireOp",EDGE,"E72.0");var subQ14=sQuery(id+"F12.wireOp",EDGE,"E72.1");var subQ16=sQuery(id+"F12.wireOp",EDGE,"E74.1");var subQ18=sQuery(id+"F12.wireOp",EDGE,"E74.8");Q0=qUnion([makeQuery(id+"F12.imprint","IMPRINT",FACE,{"disambiguationData":[TD([[makeQuery(id+"F12.imprint","IMPRINT",EDGE,{"derivedFrom":subQ7}),1.0]])]}),makeQuery(id+"F12.imprint","IMPRINT",FACE,{"disambiguationData":[TD([[makeQuery(id+"F12.imprint","IMPRINT",EDGE,{"derivedFrom":subQ14}),1.0]])]}),makeQuery(id+"F12.imprint","IMPRINT",FACE,{"disambiguationData":[TD([[makeQuery(id+"F12.imprint","IMPRINT",EDGE,{"derivedFrom":subQ16}),1.0]])]}),makeQuery(id+"F12.imprint","IMPRINT",FACE,{"disambiguationData":[TD([[makeQuery(id+"F12.imprint","IMPRINT",EDGE,{"derivedFrom":subQ18}),-1.0]])]})]);}
            var Q1;
            Q1=makeQuery(id+"F5.boolean.opBoolean","SPLIT",FACE,{"disambiguationData":[TD([makeQuery(id+"F5.opExtrude","SWEPT_FACE",FACE,{"disambiguationData":[OSD([sQuery(id+"F4.wireOp",EDGE,"E41")])]})])],"derivedFrom":makeQuery(id+"F3.boolean.opBoolean","COPY",FACE,{"derivedFrom":makeQuery(id+"F3.opExtrude","CAP_FACE",FACE,{"disambiguationData":[OSD([sQuery(id+"F0.wireOp",EDGE,"E25.0"),sQuery(id+"F0.wireOp",EDGE,"E25.1"),sQuery(id+"F0.wireOp",EDGE,"E25.2"),sQuery(id+"F0.wireOp",EDGE,"E25.3"),sQuery(id+"F0.wireOp",EDGE,"E25.4"),sQuery(id+"F0.wireOp",EDGE,"E25.5"),sQuery(id+"F0.wireOp",EDGE,"E25.6"),sQuery(id+"F0.wireOp",EDGE,"E25.7")])],"isStart":false})})});
            extrude(context, id + "F13", {"entities" : qUnion([Q0]), "operationType" : NewBodyOperationType.REMOVE, "endBound" : BoundingType.UP_TO_SURFACE, "endBoundEntityFace" : qUnion([Q1]), "depth" : 25 * mm});
        }
        {
            var Q0;
            Q0=makeQuery(id+"F3.boolean.opBoolean","COPY",EDGE,{"derivedFrom":makeQuery(id+"F3.opExtrude","CAP_EDGE",EDGE,{"disambiguationData":[OSD([sQuery(id+"F0.wireOp",EDGE,"E25.6")])],"isStart":false})});
            var Q1;
            Q1=makeQuery(id+"F8.boolean.opBoolean","INTERSECT",EDGE,{"derivedFrom":[makeQuery(id+"F5.opExtrude","SWEPT_FACE",FACE,{"disambiguationData":[OSD([sQuery(id+"F4.wireOp",EDGE,"E30")])]}),makeQuery(id+"F8.opExtrude","CAP_FACE",FACE,{"disambiguationData":[OSD([sQuery(id+"F7.wireOp",EDGE,"E67")])],"isStart":false})]});
            var Q2;
            Q2=makeQuery(id+"F8.boolean.opBoolean","INTERSECT",EDGE,{"disambiguationData":[OD(1.0)],"derivedFrom":[makeQuery(id+"F5.opExtrude","SWEPT_FACE",FACE,{"disambiguationData":[OSD([sQuery(id+"F4.wireOp",EDGE,"E30")])]}),makeQuery(id+"F8.opExtrude","SWEPT_FACE",FACE,{"disambiguationData":[OSD([sQuery(id+"F7.wireOp",EDGE,"E67")])]})]});
            var Q3;
            {var subQ0=sQuery(id+"F4.wireOp",EDGE,"E30");Q3=makeQuery(id+"F8.boolean.opBoolean","SPLIT",EDGE,{"disambiguationData":[TD([makeQuery(id+"F5.opExtrude","SWEPT_FACE",FACE,{"disambiguationData":[OSD([sQuery(id+"F4.wireOp",EDGE,"E35.filletArc")])]})])],"derivedFrom":makeQuery(id+"F5.opExtrude","CAP_EDGE",EDGE,{"disambiguationData":[OSD([subQ0])],"isStart":false})});}
            var Q4;
            {var subQ0=sQuery(id+"F0.wireOp",EDGE,"E25.7");var subQ1=sQuery(id+"F0.wireOp",EDGE,"E25.1");var subQ2=sQuery(id+"F0.wireOp",EDGE,"E25.6");var subQ3=sQuery(id+"F0.wireOp",EDGE,"E25.5");var subQ4=sQuery(id+"F0.wireOp",EDGE,"E25.4");var subQ5=sQuery(id+"F0.wireOp",EDGE,"E25.0");var subQ6=sQuery(id+"F0.wireOp",EDGE,"E25.2");var subQ7=sQuery(id+"F0.wireOp",EDGE,"E25.3");Q4=makeQuery(id+"F8.boolean.opBoolean","INTERSECT",EDGE,{"derivedFrom":[makeQuery(id+"F5.boolean.opBoolean","SPLIT",FACE,{"disambiguationData":[TD([makeQuery(id+"F2.opExtrude","SWEPT_FACE",FACE,{"disambiguationData":[OSD([subQ5])]})])],"derivedFrom":makeQuery(id+"F3.boolean.opBoolean","COPY",FACE,{"derivedFrom":makeQuery(id+"F3.opExtrude","CAP_FACE",FACE,{"disambiguationData":[OSD([subQ5,subQ1,subQ6,subQ7,subQ4,subQ3,subQ2,subQ0])],"isStart":false})})}),makeQuery(id+"F8.opExtrude","SWEPT_FACE",FACE,{"disambiguationData":[OSD([sQuery(id+"F7.wireOp",EDGE,"E67")])]})]});}
            var Q5;
            Q5=makeQuery(id+"F8.boolean.opBoolean","INTERSECT",EDGE,{"disambiguationData":[OD(0.0)],"derivedFrom":[makeQuery(id+"F5.opExtrude","SWEPT_FACE",FACE,{"disambiguationData":[OSD([sQuery(id+"F4.wireOp",EDGE,"E30")])]}),makeQuery(id+"F8.opExtrude","SWEPT_FACE",FACE,{"disambiguationData":[OSD([sQuery(id+"F7.wireOp",EDGE,"E67")])]})]});
            fillet(context, id + "F14", {"entities" : qUnion([Q0, Q1, Q2, Q3, Q4, Q5]), "radius" : 3 * mm, "tangentPropagation" : true, "allowEdgeOverflow" : false});
        }
        {
            var Q0;
            Q0=makeQuery(id+"F1.opExtrude","CAP_EDGE",EDGE,{"disambiguationData":[OSD([sQuery(id+"F0.wireOp",EDGE,"E1.bottom")])],"isStart":false});
            fillet(context, id + "F15", {"entities" : qUnion([Q0]), "radius" : 2 * mm, "tangentPropagation" : true, "allowEdgeOverflow" : false});
        }
        {
            var Q0;
            {var subQ0=sQuery(id+"F0.wireOp",EDGE,"E21.filletArc");var subQ1=sQuery(id+"F0.wireOp",EDGE,"E7");var subQ2=sQuery(id+"F0.wireOp",EDGE,"E6");var subQ3=sQuery(id+"F0.wireOp",EDGE,"E5");var subQ4=sQuery(id+"F0.wireOp",EDGE,"E4");var subQ5=sQuery(id+"F0.wireOp",EDGE,"E22.filletArc");var subQ6=sQuery(id+"F0.wireOp",EDGE,"E1.bottom");var subQ7=sQuery(id+"F0.wireOp",EDGE,"E1.right");var subQ8=sQuery(id+"F0.wireOp",EDGE,"E1.top");var subQ9=sQuery(id+"F0.wireOp",EDGE,"E1.left");var subQ10=sQuery(id+"F0.wireOp",EDGE,"E23.filletArc");var subQ11=sQuery(id+"F0.wireOp",EDGE,"E24.filletArc");Q0=makeQuery(id+"F2.boolean.opBoolean","SPLIT",FACE,{"disambiguationData":[TD([makeQuery(id+"F1.opExtrude","SWEPT_FACE",FACE,{"disambiguationData":[OSD([subQ6])]})])],"derivedFrom":makeQuery(id+"F1.opExtrude","CAP_FACE",FACE,{"disambiguationData":[OSD([subQ6,subQ8,subQ9,subQ7,subQ4,subQ3,subQ2,subQ1,subQ0,subQ5,subQ10,subQ11])],"isStart":true})});}
            var sketch = newSketch(context, id + "F16", { "sketchPlane" : qUnion([Q0])});
            skCircle(sketch, "E79", {"center": v(-104.25, 0) * mm, "radius": 6 * mm});
            skLineSegment(sketch, "E80", {"start": v(-104.25, -14.63) * mm, "end": v(-92.25, -14.63) * mm});
            skLineSegment(sketch, "E81", {"start": v(-104.25, 15.37) * mm, "end": v(-92.08, 15.37) * mm});
            skLineSegment(sketch, "E82", {"start": v(-92.08, 15.37) * mm, "end": v(-74.25, 33.2) * mm});
            skLineSegment(sketch, "E83", {"start": v(-92.25, -14.63) * mm, "end": v(-74.25, -36.48) * mm});
            skArc(sketch, "E84", {"start": v(-104.25, -14.63) * mm, "mid": v(-119.25, 0.37) * mm, "end": v(-104.25, 15.37) * mm});
            skLineSegment(sketch, "E85", {"start": v(0, 0) * mm, "end": v(0, -74.25) * mm});
            skLineSegment(sketch, "E86.bottom", {"start": v(0, 74.25) * mm, "end": v(0, 74.25) * mm});
            skLineSegment(sketch, "E86.top", {"start": v(0, -74.25) * mm, "end": v(0, -74.25) * mm});
            skLineSegment(sketch, "E86.left", {"start": v(0, 74.25) * mm, "end": v(0, -74.25) * mm});
            skPoint(sketch, "E86.middle", {"position": v(0, 0) * mm});
            skArc(sketch, "E87.MirrorCS", {"start": v(104.25, -14.63) * mm, "mid": v(119.25, 0.37) * mm, "end": v(104.25, 15.37) * mm});
            skLineSegment(sketch, "E88.MirrorCS", {"start": v(104.25, 15.37) * mm, "end": v(92.08, 15.37) * mm});
            skCircle(sketch, "E89.MirrorC", {"center": v(104.25, 0) * mm, "radius": 6 * mm});
            skLineSegment(sketch, "E90.MirrorCS", {"start": v(104.25, -14.63) * mm, "end": v(92.25, -14.63) * mm});
            skLineSegment(sketch, "E91.MirrorCS", {"start": v(92.08, 15.37) * mm, "end": v(74.25, 33.2) * mm});
            skLineSegment(sketch, "E92.MirrorCS", {"start": v(92.25, -14.63) * mm, "end": v(74.25, -36.48) * mm});
            skSolve(sketch);
        }
        {
            var Q0;
            Q0 = qSketchRegion(id + "F16", true);
            var Q1;
            Q1=makeQuery(id+"F16.imprint","IMPRINT",FACE,{"disambiguationData":[TD([[makeQuery(id+"F16.imprint","IMPRINT",EDGE,{"derivedFrom":sQuery(id+"F16.wireOp",EDGE,"E79")}),-1.0]])]});
            var Q2;
            Q2=makeQuery(id+"F16.imprint","IMPRINT",FACE,{"disambiguationData":[TD([[makeQuery(id+"F16.imprint","IMPRINT",EDGE,{"derivedFrom":makeQuery(id+"F1.opExtrude","CAP_EDGE",EDGE,{"disambiguationData":[OSD([sQuery(id+"F0.wireOp",EDGE,"E4")])],"isStart":true})}),-1.0]])]});
            var Q3;
            Q3=makeQuery(id+"F16.imprint","IMPRINT",FACE,{"disambiguationData":[TD([[makeQuery(id+"F16.imprint","IMPRINT",EDGE,{"derivedFrom":makeQuery(id+"F1.opExtrude","CAP_EDGE",EDGE,{"disambiguationData":[OSD([sQuery(id+"F0.wireOp",EDGE,"E5")])],"isStart":true})}),-1.0]])]});
            var Q4;
            Q4=makeQuery(id+"F16.imprint","IMPRINT",FACE,{"disambiguationData":[TD([[makeQuery(id+"F16.imprint","IMPRINT",EDGE,{"derivedFrom":sQuery(id+"F16.wireOp",EDGE,"E87.MirrorCS")}),1.0]])]});
            var Q5;
            Q5=makeQuery(id+"F2.opExtrude","CAP_FACE",FACE,{"disambiguationData":[OSD([sQuery(id+"F0.wireOp",EDGE,"E12"),sQuery(id+"F0.wireOp",EDGE,"E13"),sQuery(id+"F0.wireOp",EDGE,"E14"),sQuery(id+"F0.wireOp",EDGE,"E15"),sQuery(id+"F0.wireOp",EDGE,"E17.filletArc"),sQuery(id+"F0.wireOp",EDGE,"E18.filletArc"),sQuery(id+"F0.wireOp",EDGE,"E19.filletArc"),sQuery(id+"F0.wireOp",EDGE,"E20.filletArc"),sQuery(id+"F0.wireOp",EDGE,"E25.0"),sQuery(id+"F0.wireOp",EDGE,"E25.1"),sQuery(id+"F0.wireOp",EDGE,"E25.2"),sQuery(id+"F0.wireOp",EDGE,"E25.3"),sQuery(id+"F0.wireOp",EDGE,"E25.4"),sQuery(id+"F0.wireOp",EDGE,"E25.5"),sQuery(id+"F0.wireOp",EDGE,"E25.6"),sQuery(id+"F0.wireOp",EDGE,"E25.7")])],"isStart":false});
            extrude(context, id + "F17", {"entities" : qUnion([Q0, Q1, Q2, Q3, Q4]), "operationType" : NewBodyOperationType.ADD, "endBound" : BoundingType.UP_TO_SURFACE, "depth" : 25 * mm, "endBoundEntityFace" : qUnion([Q5]), "offsetDistance" : 25 * mm});
        }
    });
